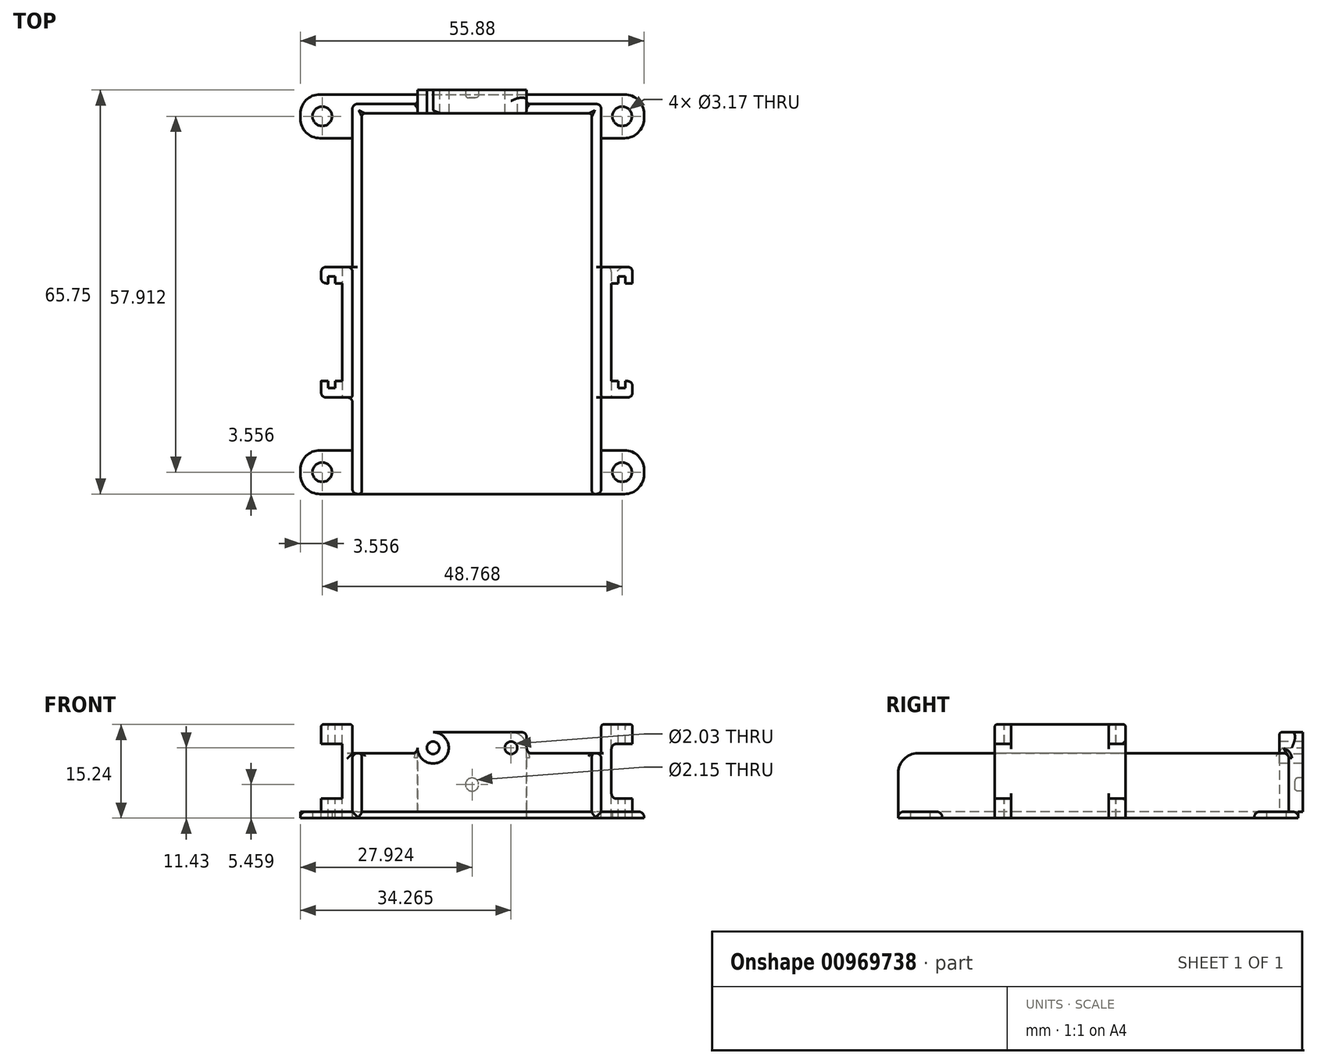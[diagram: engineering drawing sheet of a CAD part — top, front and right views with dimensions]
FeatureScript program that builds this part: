
annotation { "Feature Type Name" : "Feature", "Feature Type Description" : "" }
export const myFeature = defineFeature(function(context is Context, id is Id, definition is map)
    precondition{}
    {
        {
            var Q0;
            Q0=qCreatedBy(makeId("Top.planeOp"),FACE);
            var sketch = newSketch(context, id + "F0", { "sketchPlane" : qUnion([Q0])});
            skLineSegment(sketch, "E0", {"start": v(0, -32.35) * mm, "end": v(-27.94, -32.35) * mm});
            skLineSegment(sketch, "E1", {"start": v(-27.94, -32.35) * mm, "end": v(-27.94, -25.24) * mm});
            skLineSegment(sketch, "E2", {"start": v(-27.94, 32.67) * mm, "end": v(27.94, 32.67) * mm});
            skLineSegment(sketch, "E3", {"start": v(27.94, 32.67) * mm, "end": v(27.94, 25.56) * mm});
            skLineSegment(sketch, "E4", {"start": v(27.94, -32.35) * mm, "end": v(0, -32.35) * mm});
            skLineSegment(sketch, "E5", {"start": v(0, -32.35) * mm, "end": v(0, 32.67) * mm, "construction": true});
            skLineSegment(sketch, "E6", {"start": v(-29.38, 29.12) * mm, "end": v(30.41, 29.12) * mm, "construction": true});
            skLineSegment(sketch, "E7", {"start": v(-30.17, -28.8) * mm, "end": v(31.36, -28.8) * mm, "construction": true});
            skLineSegment(sketch, "E8", {"start": v(-24.38, 34.73) * mm, "end": v(-24.38, -35.44) * mm, "construction": true});
            skLineSegment(sketch, "E9", {"start": v(24.38, 35.22) * mm, "end": v(24.38, -36.91) * mm, "construction": true});
            skCircle(sketch, "E10", {"center": v(-24.38, 29.12) * mm, "radius": 1.59 * mm});
            skCircle(sketch, "E11", {"center": v(24.38, 29.12) * mm, "radius": 1.59 * mm});
            skCircle(sketch, "E12", {"center": v(-24.38, -28.8) * mm, "radius": 1.59 * mm});
            skCircle(sketch, "E13", {"center": v(24.38, -28.8) * mm, "radius": 1.59 * mm});
            skLineSegment(sketch, "E14.MirrorCS", {"start": v(27.94, -25.24) * mm, "end": v(21, -25.24) * mm});
            skLineSegment(sketch, "E15.MirrorCS", {"start": v(-27.94, 25.56) * mm, "end": v(-19.47, 25.56) * mm});
            skLineSegment(sketch, "E16", {"start": v(21, -25.24) * mm, "end": v(21, 25.56) * mm});
            skLineSegment(sketch, "E17", {"start": v(-19.47, 25.56) * mm, "end": v(-19.47, -25.24) * mm});
            skLineSegment(sketch, "E18.trimOffspring", {"start": v(-27.94, 25.56) * mm, "end": v(-27.94, 32.67) * mm});
            skLineSegment(sketch, "E19.trimOffspring", {"start": v(27.94, -25.24) * mm, "end": v(27.94, -32.35) * mm});
            skLineSegment(sketch, "E20.trimOffspring", {"start": v(21, 25.56) * mm, "end": v(27.94, 25.56) * mm});
            skLineSegment(sketch, "E21", {"start": v(-27.94, -25.24) * mm, "end": v(-19.47, -25.24) * mm});
            skSolve(sketch);
        }
        {
            var Q0;
            Q0 = qSketchRegion(id + "F0", true);
            extrude(context, id + "F1", {"entities" : qUnion([Q0]), "depth" : 1.02 * mm, "offsetDistance" : 25.4 * mm});
        }
        {
            var Q0;
            Q0=makeQuery(id+"F1.opExtrude","CAP_FACE",FACE,{"disambiguationData":[OSD([sQuery(id+"F0.wireOp",EDGE,"E0"),sQuery(id+"F0.wireOp",EDGE,"E1"),sQuery(id+"F0.wireOp",EDGE,"E2"),sQuery(id+"F0.wireOp",EDGE,"E3"),sQuery(id+"F0.wireOp",EDGE,"E4"),sQuery(id+"F0.wireOp",EDGE,"E10"),sQuery(id+"F0.wireOp",EDGE,"E11"),sQuery(id+"F0.wireOp",EDGE,"E12"),sQuery(id+"F0.wireOp",EDGE,"E13"),sQuery(id+"F0.wireOp",EDGE,"E14.MirrorCS"),sQuery(id+"F0.wireOp",EDGE,"E15.MirrorCS"),sQuery(id+"F0.wireOp",EDGE,"E16"),sQuery(id+"F0.wireOp",EDGE,"E17"),sQuery(id+"F0.wireOp",EDGE,"E18.trimOffspring"),sQuery(id+"F0.wireOp",EDGE,"E19.trimOffspring"),sQuery(id+"F0.wireOp",EDGE,"E20.trimOffspring"),sQuery(id+"F0.wireOp",EDGE,"E21")])],"isStart":false});
            var sketch = newSketch(context, id + "F2", { "sketchPlane" : qUnion([Q0])});
            skLineSegment(sketch, "E22", {"start": v(-19.47, 0) * mm, "end": v(-19.47, 31.13) * mm});
            skLineSegment(sketch, "E23", {"start": v(21, 0.16) * mm, "end": v(21, 31.13) * mm});
            skLineSegment(sketch, "E24", {"start": v(-19.47, 0) * mm, "end": v(-19.47, -32.35) * mm});
            skLineSegment(sketch, "E25", {"start": v(-19.47, -32.35) * mm, "end": v(-17.94, -32.35) * mm});
            skLineSegment(sketch, "E26", {"start": v(-17.94, -32.35) * mm, "end": v(-17.94, 29.59) * mm});
            skLineSegment(sketch, "E27", {"start": v(-17.94, 29.59) * mm, "end": v(19.47, 29.59) * mm});
            skLineSegment(sketch, "E28", {"start": v(19.47, 29.59) * mm, "end": v(19.47, -32.35) * mm});
            skLineSegment(sketch, "E29", {"start": v(19.47, -32.35) * mm, "end": v(21, -32.35) * mm});
            skLineSegment(sketch, "E30", {"start": v(21, -32.35) * mm, "end": v(21, 0.16) * mm});
            skLineSegment(sketch, "E31", {"start": v(0, 31.13) * mm, "end": v(-19.47, 31.13) * mm});
            skLineSegment(sketch, "E32", {"start": v(-19.47, 31.13) * mm, "end": v(0, 31.13) * mm});
            skLineSegment(sketch, "E33", {"start": v(0, 31.13) * mm, "end": v(21, 31.13) * mm});
            skSolve(sketch);
        }
        {
            var Q0;
            {var subQ0=sQuery(id+"F2.wireOp",EDGE,"E25");Q0=makeQuery(id+"F2.imprint","IMPRINT",FACE,{"disambiguationData":[TD([[makeQuery(id+"F2.imprint","IMPRINT",EDGE,{"derivedFrom":subQ0}),-1.0]])]});}
            extrude(context, id + "F3", {"entities" : qUnion([Q0]), "operationType" : NewBodyOperationType.ADD, "depth" : 9.52 * mm, "offsetDistance" : 25.4 * mm});
        }
        {
            var Q0;
            Q0=makeQuery(id+"F3.boolean.opBoolean","MERGE",FACE,{"derivedFrom":[makeQuery(id+"F1.opExtrude","SWEPT_FACE",FACE,{"disambiguationData":[OSD([sQuery(id+"F0.wireOp",EDGE,"E17")])]}),makeQuery(id+"F3.opExtrude","SWEPT_FACE",FACE,{"disambiguationData":[OSD([sQuery(id+"F2.wireOp",EDGE,"E22"),sQuery(id+"F2.wireOp",EDGE,"E24")])]})]});
            var sketch = newSketch(context, id + "F4", { "sketchPlane" : qUnion([Q0])});
            skLineSegment(sketch, "E34.bottom", {"start": v(16.65, 0) * mm, "end": v(-4.6, 0) * mm});
            skLineSegment(sketch, "E34.top", {"start": v(16.65, 15.24) * mm, "end": v(-4.6, 15.24) * mm});
            skLineSegment(sketch, "E34.left", {"start": v(16.65, 0) * mm, "end": v(16.65, 15.24) * mm});
            skLineSegment(sketch, "E34.right", {"start": v(-4.6, 0) * mm, "end": v(-4.6, 15.24) * mm});
            skSolve(sketch);
        }
        {
            var Q0;
            {var subQ0=sQuery(id+"F4.wireOp",EDGE,"E34.top");Q0=makeQuery(id+"F4.imprint","IMPRINT",FACE,{"disambiguationData":[TD([[makeQuery(id+"F4.imprint","IMPRINT",EDGE,{"derivedFrom":subQ0}),1.0]])]});}
            var Q1;
            {var subQ1=sQuery(id+"F4.wireOp",EDGE,"E34.bottom");Q1=makeQuery(id+"F4.imprint","IMPRINT",FACE,{"disambiguationData":[TD([[makeQuery(id+"F4.imprint","IMPRINT",EDGE,{"derivedFrom":subQ1}),1.0]])]});}
            extrude(context, id + "F5", {"entities" : qUnion([Q0, Q1]), "operationType" : NewBodyOperationType.ADD, "depth" : 5.08 * mm, "offsetDistance" : 25.4 * mm});
        }
        {
            var Q0;
            Q0=makeQuery(id+"F5.opExtrude","SWEPT_FACE",FACE,{"disambiguationData":[OSD([sQuery(id+"F4.wireOp",EDGE,"E34.top")])]});
            var sketch = newSketch(context, id + "F6", { "sketchPlane" : qUnion([Q0])});
            skLineSegment(sketch, "E35", {"start": v(-24.55, 1.94) * mm, "end": v(-23.4, 1.94) * mm});
            skLineSegment(sketch, "E36", {"start": v(-23.4, 1.94) * mm, "end": v(-23.4, 3.08) * mm});
            skLineSegment(sketch, "E37", {"start": v(-23.4, 3.08) * mm, "end": v(-22.26, 3.08) * mm});
            skLineSegment(sketch, "E38", {"start": v(-22.26, 3.08) * mm, "end": v(-22.26, 1.94) * mm});
            skLineSegment(sketch, "E39", {"start": v(-22.26, 1.94) * mm, "end": v(-21.12, 1.94) * mm});
            skLineSegment(sketch, "E40", {"start": v(-21.12, 1.94) * mm, "end": v(-21.12, -13.94) * mm});
            skLineSegment(sketch, "E41", {"start": v(-21.12, -13.94) * mm, "end": v(-22.26, -13.94) * mm});
            skLineSegment(sketch, "E42", {"start": v(-22.26, -13.94) * mm, "end": v(-22.26, -15.08) * mm});
            skLineSegment(sketch, "E43", {"start": v(-22.26, -15.08) * mm, "end": v(-23.4, -15.08) * mm});
            skLineSegment(sketch, "E44", {"start": v(-23.4, -15.08) * mm, "end": v(-23.4, -13.94) * mm});
            skLineSegment(sketch, "E45", {"start": v(-23.4, -13.94) * mm, "end": v(-24.55, -13.94) * mm});
            skLineSegment(sketch, "E46", {"start": v(-24.55, -13.94) * mm, "end": v(-24.55, 1.94) * mm});
            skSolve(sketch);
        }
        {
            var Q0;
            Q0=makeQuery(id+"F6.imprint","IMPRINT",FACE,{"disambiguationData":[TD([[makeQuery(id+"F6.imprint","IMPRINT",EDGE,{"derivedFrom":sQuery(id+"F6.wireOp",EDGE,"E35")}),-1.0]])]});
            extrude(context, id + "F7", {"entities" : qUnion([Q0]), "operationType" : NewBodyOperationType.REMOVE, "oppositeDirection" : true, "depth" : 15.24 * mm, "offsetDistance" : 25.4 * mm});
        }
        {
            var Q0;
            Q0=makeQuery(id+"F3.opExtrude","SWEPT_FACE",FACE,{"disambiguationData":[OSD([sQuery(id+"F2.wireOp",EDGE,"E27")])]});
            var sketch = newSketch(context, id + "F8", { "sketchPlane" : qUnion([Q0])});
            skLineSegment(sketch, "E47", {"start": v(0.76, 1.02) * mm, "end": v(8.86, 1.02) * mm});
            skLineSegment(sketch, "E48", {"start": v(8.86, 1.02) * mm, "end": v(8.86, 13.97) * mm});
            skLineSegment(sketch, "E49", {"start": v(8.86, 13.97) * mm, "end": v(-8.9, 13.97) * mm});
            skLineSegment(sketch, "E50", {"start": v(-8.9, 13.97) * mm, "end": v(-8.9, 1.02) * mm});
            skLineSegment(sketch, "E51", {"start": v(-8.9, 1.02) * mm, "end": v(0.76, 1.02) * mm});
            skSolve(sketch);
        }
        {
            var Q0;
            {var subQ2=sQuery(id+"F8.wireOp",EDGE,"E47");Q0=makeQuery(id+"F8.imprint","IMPRINT",FACE,{"disambiguationData":[TD([[makeQuery(id+"F8.imprint","IMPRINT",EDGE,{"derivedFrom":subQ2}),1.0]])]});}
            var Q1;
            {var subQ0=sQuery(id+"F8.wireOp",EDGE,"E49");Q1=makeQuery(id+"F8.imprint","IMPRINT",FACE,{"disambiguationData":[TD([[makeQuery(id+"F8.imprint","IMPRINT",EDGE,{"derivedFrom":subQ0}),1.0]])]});}
            extrude(context, id + "F9", {"entities" : qUnion([Q0, Q1]), "operationType" : NewBodyOperationType.ADD, "depth" : -2.54 * mm, "offsetDistance" : 25.4 * mm});
        }
        {
            var Q0;
            Q0=makeQuery(id+"F9.opExtrude","CAP_FACE",FACE,{"disambiguationData":[OSD([sQuery(id+"F8.wireOp",EDGE,"E47"),sQuery(id+"F8.wireOp",EDGE,"E48"),sQuery(id+"F8.wireOp",EDGE,"E49"),sQuery(id+"F8.wireOp",EDGE,"E50"),sQuery(id+"F8.wireOp",EDGE,"E51")])],"isStart":false});
            var sketch = newSketch(context, id + "F10", { "sketchPlane" : qUnion([Q0])});
            skCircle(sketch, "E52", {"center": v(-6.32, 11.43) * mm, "radius": 1.02 * mm});
            skCircle(sketch, "E53", {"center": v(-6.32, 11.43) * mm, "radius": 2.54 * mm});
            skLineSegment(sketch, "E54", {"start": v(0.02, 13.97) * mm, "end": v(0.02, 1.02) * mm});
            skCircle(sketch, "E55", {"center": v(0.02, 5.46) * mm, "radius": 1.08 * mm});
            skCircle(sketch, "E56.MirrorC", {"center": v(6.36, 11.43) * mm, "radius": 1.02 * mm});
            skCircle(sketch, "E57.MirrorC", {"center": v(6.36, 11.43) * mm, "radius": 2.54 * mm});
            skSolve(sketch);
        }
        {
            var Q0;
            Q0=makeQuery(id+"F10.imprint","IMPRINT",FACE,{"disambiguationData":[TD([[makeQuery(id+"F10.imprint","IMPRINT",EDGE,{"derivedFrom":sQuery(id+"F10.wireOp",EDGE,"E52")}),-1.0]])]});
            var Q1;
            Q1=makeQuery(id+"F10.imprint","IMPRINT",FACE,{"disambiguationData":[TD([[makeQuery(id+"F10.imprint","IMPRINT",EDGE,{"derivedFrom":sQuery(id+"F10.wireOp",EDGE,"E56.MirrorC")}),1.0]])]});
            var Q2;
            {var subQ0=sQuery(id+"F10.wireOp",EDGE,"E55");var subQ1=sQuery(id+"F10.wireOp",EDGE,"E54");var subQ2=makeQuery(id+"F10.imprint","INTERSECT",VERTEX,{"disambiguationData":[OD(0.0)],"derivedFrom":[subQ1,subQ0]});Q2=makeQuery(id+"F10.imprint","IMPRINT",FACE,{"disambiguationData":[TD([[makeQuery(id+"F10.imprint","IMPRINT",EDGE,{"disambiguationData":[TD([[subQ2,-1.0]])],"derivedFrom":subQ1}),1.0]])]});}
            var Q3;
            {var subQ0=sQuery(id+"F10.wireOp",EDGE,"E55");var subQ1=sQuery(id+"F10.wireOp",EDGE,"E54");var subQ2=makeQuery(id+"F10.imprint","INTERSECT",VERTEX,{"disambiguationData":[OD(0.0)],"derivedFrom":[subQ1,subQ0]});Q3=makeQuery(id+"F10.imprint","IMPRINT",FACE,{"disambiguationData":[TD([[makeQuery(id+"F10.imprint","IMPRINT",EDGE,{"disambiguationData":[TD([[subQ2,-1.0]])],"derivedFrom":subQ1}),-1.0]])]});}
            extrude(context, id + "F11", {"entities" : qUnion([Q0, Q1, Q2, Q3]), "operationType" : NewBodyOperationType.ADD, "depth" : 1.27 * mm, "offsetDistance" : 25.4 * mm});
        }
        {
            var Q0;
            Q0=makeQuery(id+"F11.boolean.opBoolean","SPLIT",FACE,{"disambiguationData":[TD([makeQuery(id+"F11.opExtrude","SWEPT_FACE",FACE,{"disambiguationData":[OSD([sQuery(id+"F10.wireOp",EDGE,"E52")])]})])],"derivedFrom":makeQuery(id+"F9.opExtrude","CAP_FACE",FACE,{"disambiguationData":[OSD([sQuery(id+"F8.wireOp",EDGE,"E47"),sQuery(id+"F8.wireOp",EDGE,"E48"),sQuery(id+"F8.wireOp",EDGE,"E49"),sQuery(id+"F8.wireOp",EDGE,"E50"),sQuery(id+"F8.wireOp",EDGE,"E51")])],"isStart":false})});
            var Q1;
            Q1=makeQuery(id+"F11.boolean.opBoolean","SPLIT",FACE,{"disambiguationData":[TD([makeQuery(id+"F11.opExtrude","SWEPT_FACE",FACE,{"disambiguationData":[OSD([sQuery(id+"F10.wireOp",EDGE,"E56.MirrorC")])]})])],"derivedFrom":makeQuery(id+"F9.opExtrude","CAP_FACE",FACE,{"disambiguationData":[OSD([sQuery(id+"F8.wireOp",EDGE,"E47"),sQuery(id+"F8.wireOp",EDGE,"E48"),sQuery(id+"F8.wireOp",EDGE,"E49"),sQuery(id+"F8.wireOp",EDGE,"E50"),sQuery(id+"F8.wireOp",EDGE,"E51")])],"isStart":false})});
            extrude(context, id + "F12", {"entities" : qUnion([Q0, Q1]), "operationType" : NewBodyOperationType.REMOVE, "oppositeDirection" : true, "depth" : 2.54 * mm, "offsetDistance" : 25.4 * mm});
        }
        {
            var Q0;
            Q0=makeQuery(id+"F1.opExtrude","SWEPT_EDGE",EDGE,{"disambiguationData":[OSD([sQuery(id+"F0.wireOp",EDGE,"E2"),sQuery(id+"F0.wireOp",EDGE,"E18.trimOffspring")])]});
            var Q1;
            Q1=makeQuery(id+"F1.opExtrude","SWEPT_EDGE",EDGE,{"disambiguationData":[OSD([sQuery(id+"F0.wireOp",EDGE,"E15.MirrorCS"),sQuery(id+"F0.wireOp",EDGE,"E18.trimOffspring")])]});
            var Q2;
            Q2=makeQuery(id+"F1.opExtrude","SWEPT_EDGE",EDGE,{"disambiguationData":[OSD([sQuery(id+"F0.wireOp",EDGE,"E3"),sQuery(id+"F0.wireOp",EDGE,"E20.trimOffspring")])]});
            var Q3;
            Q3=makeQuery(id+"F1.opExtrude","SWEPT_EDGE",EDGE,{"disambiguationData":[OSD([sQuery(id+"F0.wireOp",EDGE,"E2"),sQuery(id+"F0.wireOp",EDGE,"E3")])]});
            var Q4;
            Q4=makeQuery(id+"F1.opExtrude","SWEPT_EDGE",EDGE,{"disambiguationData":[OSD([sQuery(id+"F0.wireOp",EDGE,"E4"),sQuery(id+"F0.wireOp",EDGE,"E19.trimOffspring")])]});
            var Q5;
            Q5=makeQuery(id+"F1.opExtrude","SWEPT_EDGE",EDGE,{"disambiguationData":[OSD([sQuery(id+"F0.wireOp",EDGE,"E14.MirrorCS"),sQuery(id+"F0.wireOp",EDGE,"E19.trimOffspring")])]});
            var Q6;
            Q6=makeQuery(id+"F1.opExtrude","SWEPT_EDGE",EDGE,{"disambiguationData":[OSD([sQuery(id+"F0.wireOp",EDGE,"E1"),sQuery(id+"F0.wireOp",EDGE,"E21")])]});
            var Q7;
            Q7=makeQuery(id+"F1.opExtrude","SWEPT_EDGE",EDGE,{"disambiguationData":[OSD([sQuery(id+"F0.wireOp",EDGE,"E0"),sQuery(id+"F0.wireOp",EDGE,"E1")])]});
            fillet(context, id + "F13", {"entities" : qUnion([Q0, Q1, Q2, Q3, Q4, Q5, Q6, Q7]), "radius" : 3.17 * mm, "tangentPropagation" : true, "allowEdgeOverflow" : false});
        }
        {
            var Q0;
            Q0=makeQuery(id+"F5.opExtrude","SWEPT_FACE",FACE,{"disambiguationData":[OSD([sQuery(id+"F4.wireOp",EDGE,"E34.left")])]});
            var sketch = newSketch(context, id + "F14", { "sketchPlane" : qUnion([Q0])});
            skLineSegment(sketch, "E58.bottom", {"start": v(-24.55, 12.07) * mm, "end": v(-21.12, 12.07) * mm});
            skLineSegment(sketch, "E58.top", {"start": v(-24.55, 3.17) * mm, "end": v(-21.12, 3.17) * mm});
            skLineSegment(sketch, "E58.left", {"start": v(-24.55, 12.07) * mm, "end": v(-24.55, 3.17) * mm});
            skLineSegment(sketch, "E58.right", {"start": v(-21.12, 12.07) * mm, "end": v(-21.12, 3.17) * mm});
            skSolve(sketch);
        }
        {
            var Q0;
            Q0=makeQuery(id+"F14.imprint","IMPRINT",FACE,{"disambiguationData":[TD([[makeQuery(id+"F14.imprint","IMPRINT",EDGE,{"derivedFrom":sQuery(id+"F14.wireOp",EDGE,"E58.bottom")}),-1.0]])]});
            extrude(context, id + "F15", {"entities" : qUnion([Q0]), "operationType" : NewBodyOperationType.REMOVE, "oppositeDirection" : true, "depth" : 25.4 * mm, "offsetDistance" : 25.4 * mm});
        }
        {
            var Q0;
            Q0=makeQuery(id+"F3.boolean.opBoolean","MERGE",FACE,{"derivedFrom":[makeQuery(id+"F1.opExtrude","SWEPT_FACE",FACE,{"disambiguationData":[OSD([sQuery(id+"F0.wireOp",EDGE,"E16")])]}),makeQuery(id+"F3.opExtrude","SWEPT_FACE",FACE,{"disambiguationData":[OSD([sQuery(id+"F2.wireOp",EDGE,"E23"),sQuery(id+"F2.wireOp",EDGE,"E30")])]})]});
            var sketch = newSketch(context, id + "F16", { "sketchPlane" : qUnion([Q0])});
            skLineSegment(sketch, "E59.bottom", {"start": v(-16.65, 0) * mm, "end": v(4.6, 0) * mm});
            skLineSegment(sketch, "E59.top", {"start": v(-16.65, 15.24) * mm, "end": v(4.6, 15.24) * mm});
            skLineSegment(sketch, "E59.left", {"start": v(-16.65, 0) * mm, "end": v(-16.65, 15.24) * mm});
            skLineSegment(sketch, "E59.right", {"start": v(4.6, 0) * mm, "end": v(4.6, 15.24) * mm});
            skSolve(sketch);
        }
        {
            var Q0;
            {var subQ0=sQuery(id+"F16.wireOp",EDGE,"E59.bottom");Q0=makeQuery(id+"F16.imprint","IMPRINT",FACE,{"disambiguationData":[TD([[makeQuery(id+"F16.imprint","IMPRINT",EDGE,{"derivedFrom":subQ0}),1.0]])]});}
            var Q1;
            {var subQ0=sQuery(id+"F16.wireOp",EDGE,"E59.top");Q1=makeQuery(id+"F16.imprint","IMPRINT",FACE,{"disambiguationData":[TD([[makeQuery(id+"F16.imprint","IMPRINT",EDGE,{"derivedFrom":subQ0}),-1.0]])]});}
            extrude(context, id + "F17", {"entities" : qUnion([Q0, Q1]), "operationType" : NewBodyOperationType.ADD, "depth" : 5.08 * mm, "offsetDistance" : 25.4 * mm});
        }
        {
            var Q0;
            Q0=makeQuery(id+"F17.opExtrude","SWEPT_FACE",FACE,{"disambiguationData":[OSD([sQuery(id+"F16.wireOp",EDGE,"E59.top")])]});
            var sketch = newSketch(context, id + "F18", { "sketchPlane" : qUnion([Q0])});
            skLineSegment(sketch, "E60", {"start": v(26.07, -13.99) * mm, "end": v(24.93, -13.99) * mm});
            skLineSegment(sketch, "E61", {"start": v(24.93, -13.99) * mm, "end": v(24.93, -15.13) * mm});
            skLineSegment(sketch, "E62", {"start": v(24.93, -15.13) * mm, "end": v(23.79, -15.13) * mm});
            skLineSegment(sketch, "E63", {"start": v(23.79, -15.13) * mm, "end": v(23.79, -13.99) * mm});
            skLineSegment(sketch, "E64", {"start": v(23.79, -13.99) * mm, "end": v(22.64, -13.99) * mm});
            skLineSegment(sketch, "E65", {"start": v(22.64, -13.99) * mm, "end": v(22.64, 1.89) * mm});
            skLineSegment(sketch, "E66", {"start": v(22.64, 1.89) * mm, "end": v(23.79, 1.89) * mm});
            skLineSegment(sketch, "E67", {"start": v(23.79, 1.89) * mm, "end": v(23.79, 3.03) * mm});
            skLineSegment(sketch, "E68", {"start": v(23.79, 3.03) * mm, "end": v(24.93, 3.03) * mm});
            skLineSegment(sketch, "E69", {"start": v(24.93, 3.03) * mm, "end": v(24.93, 1.89) * mm});
            skLineSegment(sketch, "E70", {"start": v(24.93, 1.89) * mm, "end": v(26.07, 1.89) * mm});
            skLineSegment(sketch, "E71", {"start": v(26.07, 1.89) * mm, "end": v(26.07, -13.99) * mm});
            skSolve(sketch);
        }
        {
            var Q0;
            Q0=makeQuery(id+"F18.imprint","IMPRINT",FACE,{"disambiguationData":[TD([[makeQuery(id+"F18.imprint","IMPRINT",EDGE,{"derivedFrom":sQuery(id+"F18.wireOp",EDGE,"E60")}),-1.0]])]});
            extrude(context, id + "F19", {"entities" : qUnion([Q0]), "operationType" : NewBodyOperationType.REMOVE, "oppositeDirection" : true, "depth" : 25.4 * mm, "offsetDistance" : 25.4 * mm});
        }
        {
            var Q0;
            Q0=makeQuery(id+"F17.opExtrude","SWEPT_FACE",FACE,{"disambiguationData":[OSD([sQuery(id+"F16.wireOp",EDGE,"E59.left")])]});
            var sketch = newSketch(context, id + "F20", { "sketchPlane" : qUnion([Q0])});
            skLineSegment(sketch, "E72.bottom", {"start": v(26.07, 12.07) * mm, "end": v(22.64, 12.07) * mm});
            skLineSegment(sketch, "E72.top", {"start": v(26.07, 3.18) * mm, "end": v(22.64, 3.18) * mm});
            skLineSegment(sketch, "E72.left", {"start": v(26.07, 12.07) * mm, "end": v(26.07, 3.18) * mm});
            skLineSegment(sketch, "E72.right", {"start": v(22.64, 12.07) * mm, "end": v(22.64, 3.18) * mm});
            skSolve(sketch);
        }
        {
            var Q0;
            Q0=makeQuery(id+"F20.imprint","IMPRINT",FACE,{"disambiguationData":[TD([[makeQuery(id+"F20.imprint","IMPRINT",EDGE,{"derivedFrom":sQuery(id+"F20.wireOp",EDGE,"E72.bottom")}),1.0]])]});
            extrude(context, id + "F21", {"entities" : qUnion([Q0]), "operationType" : NewBodyOperationType.REMOVE, "oppositeDirection" : true, "depth" : 25.4 * mm, "offsetDistance" : 25.4 * mm});
        }
        {
            var Q0;
            Q0=makeQuery(id+"F3.opExtrude","CAP_EDGE",EDGE,{"disambiguationData":[OSD([sQuery(id+"F2.wireOp",EDGE,"E29")])],"isStart":false});
            var Q1;
            Q1=makeQuery(id+"F3.opExtrude","CAP_EDGE",EDGE,{"disambiguationData":[OSD([sQuery(id+"F2.wireOp",EDGE,"E25")])],"isStart":false});
            fillet(context, id + "F22", {"entities" : qUnion([Q0, Q1]), "radius" : 3.17 * mm, "tangentPropagation" : true, "allowEdgeOverflow" : false});
        }
        {
            var Q0;
            {var subQ1=sQuery(id+"F0.wireOp",EDGE,"E16");var subQ2=sQuery(id+"F0.wireOp",EDGE,"E4");var subQ3=sQuery(id+"F0.wireOp",EDGE,"E0");Q0=makeQuery(id+"F3.boolean.opBoolean","SPLIT",EDGE,{"disambiguationData":[TD([makeQuery(id+"F1.opExtrude","SWEPT_FACE",FACE,{"disambiguationData":[OSD([subQ1])]})])],"derivedFrom":makeQuery(id+"F1.opExtrude","CAP_EDGE",EDGE,{"disambiguationData":[OSD([subQ3,subQ2])],"isStart":false})});}
            var Q1;
            Q1=makeQuery(id+"F3.opExtrude","SWEPT_EDGE",EDGE,{"disambiguationData":[OSD([sQuery(id+"F0.wireOp",EDGE,"E0"),sQuery(id+"F0.wireOp",EDGE,"E4"),sQuery(id+"F2.wireOp",EDGE,"E29"),sQuery(id+"F2.wireOp",EDGE,"E30")])]});
            var Q2;
            Q2=makeQuery(id+"F21.boolean.opBoolean","COPY",EDGE,{"derivedFrom":makeQuery(id+"F21.opExtrude","CAP_EDGE",EDGE,{"disambiguationData":[OSD([sQuery(id+"F20.wireOp",EDGE,"E72.right")])],"isStart":true})});
            var Q3;
            {var subQ0=sQuery(id+"F16.wireOp",EDGE,"E59.left");Q3=makeQuery(id+"F21.boolean.opBoolean","SPLIT",EDGE,{"disambiguationData":[TD([makeQuery(id+"F5.opExtrude","SWEPT_FACE",FACE,{"disambiguationData":[OSD([sQuery(id+"F4.wireOp",EDGE,"E34.bottom")])]})])],"derivedFrom":makeQuery(id+"F17.opExtrude","CAP_EDGE",EDGE,{"disambiguationData":[OSD([subQ0])],"isStart":false})});}
            var Q4;
            {var subQ0=sQuery(id+"F16.wireOp",EDGE,"E59.top");var subQ2=sQuery(id+"F18.wireOp",EDGE,"E60");Q4=makeQuery(id+"F21.boolean.opBoolean","SPLIT",EDGE,{"disambiguationData":[TD([makeQuery(id+"F5.opExtrude","SWEPT_FACE",FACE,{"disambiguationData":[OSD([sQuery(id+"F4.wireOp",EDGE,"E34.bottom")])]})])],"derivedFrom":makeQuery(id+"F19.boolean.opBoolean","COPY",EDGE,{"derivedFrom":makeQuery(id+"F19.opExtrude","SWEPT_EDGE",EDGE,{"disambiguationData":[OSD([subQ0,subQ2,sQuery(id+"F18.wireOp",EDGE,"E71")])]})})});}
            var Q5;
            {var subQ0=sQuery(id+"F16.wireOp",EDGE,"E59.top");var subQ2=sQuery(id+"F18.wireOp",EDGE,"E70");Q5=makeQuery(id+"F21.boolean.opBoolean","SPLIT",EDGE,{"disambiguationData":[TD([makeQuery(id+"F5.opExtrude","SWEPT_FACE",FACE,{"disambiguationData":[OSD([sQuery(id+"F4.wireOp",EDGE,"E34.bottom")])]})])],"derivedFrom":makeQuery(id+"F19.boolean.opBoolean","COPY",EDGE,{"derivedFrom":makeQuery(id+"F19.opExtrude","SWEPT_EDGE",EDGE,{"disambiguationData":[OSD([subQ0,subQ2,sQuery(id+"F18.wireOp",EDGE,"E71")])]})})});}
            var Q6;
            {var subQ0=sQuery(id+"F16.wireOp",EDGE,"E59.right");Q6=makeQuery(id+"F21.boolean.opBoolean","SPLIT",EDGE,{"disambiguationData":[TD([makeQuery(id+"F5.opExtrude","SWEPT_FACE",FACE,{"disambiguationData":[OSD([sQuery(id+"F4.wireOp",EDGE,"E34.bottom")])]})])],"derivedFrom":makeQuery(id+"F17.opExtrude","CAP_EDGE",EDGE,{"disambiguationData":[OSD([subQ0])],"isStart":false})});}
            var Q7;
            Q7=makeQuery(id+"F21.boolean.opBoolean","INTERSECT",EDGE,{"derivedFrom":[makeQuery(id+"F17.opExtrude","SWEPT_FACE",FACE,{"disambiguationData":[OSD([sQuery(id+"F16.wireOp",EDGE,"E59.right")])]}),makeQuery(id+"F21.opExtrude","SWEPT_FACE",FACE,{"disambiguationData":[OSD([sQuery(id+"F20.wireOp",EDGE,"E72.right")])]})]});
            var Q8;
            {var subQ0=sQuery(id+"F16.wireOp",EDGE,"E59.right");var subQ1=sQuery(id+"F16.wireOp",EDGE,"E59.top");Q8=makeQuery(id+"F21.boolean.opBoolean","SPLIT",EDGE,{"disambiguationData":[TD([makeQuery(id+"F17.opExtrude","SWEPT_FACE",FACE,{"disambiguationData":[OSD([subQ1])]})])],"derivedFrom":makeQuery(id+"F17.opExtrude","CAP_EDGE",EDGE,{"disambiguationData":[OSD([subQ0])],"isStart":false})});}
            var Q9;
            {var subQ0=sQuery(id+"F16.wireOp",EDGE,"E59.top");var subQ1=sQuery(id+"F18.wireOp",EDGE,"E70");Q9=makeQuery(id+"F21.boolean.opBoolean","SPLIT",EDGE,{"disambiguationData":[TD([makeQuery(id+"F17.opExtrude","SWEPT_FACE",FACE,{"disambiguationData":[OSD([subQ0])]})])],"derivedFrom":makeQuery(id+"F19.boolean.opBoolean","COPY",EDGE,{"derivedFrom":makeQuery(id+"F19.opExtrude","SWEPT_EDGE",EDGE,{"disambiguationData":[OSD([subQ0,subQ1,sQuery(id+"F18.wireOp",EDGE,"E71")])]})})});}
            var Q10;
            {var subQ0=sQuery(id+"F16.wireOp",EDGE,"E59.top");var subQ1=sQuery(id+"F18.wireOp",EDGE,"E60");Q10=makeQuery(id+"F21.boolean.opBoolean","SPLIT",EDGE,{"disambiguationData":[TD([makeQuery(id+"F17.opExtrude","SWEPT_FACE",FACE,{"disambiguationData":[OSD([subQ0])]})])],"derivedFrom":makeQuery(id+"F19.boolean.opBoolean","COPY",EDGE,{"derivedFrom":makeQuery(id+"F19.opExtrude","SWEPT_EDGE",EDGE,{"disambiguationData":[OSD([subQ0,subQ1,sQuery(id+"F18.wireOp",EDGE,"E71")])]})})});}
            var Q11;
            {var subQ0=sQuery(id+"F16.wireOp",EDGE,"E59.left");var subQ1=sQuery(id+"F16.wireOp",EDGE,"E59.top");Q11=makeQuery(id+"F21.boolean.opBoolean","SPLIT",EDGE,{"disambiguationData":[TD([makeQuery(id+"F17.opExtrude","SWEPT_FACE",FACE,{"disambiguationData":[OSD([subQ1])]})])],"derivedFrom":makeQuery(id+"F17.opExtrude","CAP_EDGE",EDGE,{"disambiguationData":[OSD([subQ0])],"isStart":false})});}
            var Q12;
            {var subQ0=sQuery(id+"F20.wireOp",EDGE,"E72.top");var subQ1=sQuery(id+"F20.wireOp",EDGE,"E72.right");Q12=makeQuery(id+"F21.boolean.opBoolean","COPY",EDGE,{"disambiguationData":[TD([makeQuery(id+"F17.opExtrude","SWEPT_FACE",FACE,{"disambiguationData":[OSD([sQuery(id+"F16.wireOp",EDGE,"E59.left")])]})])],"derivedFrom":makeQuery(id+"F21.opExtrude","SWEPT_EDGE",EDGE,{"disambiguationData":[OSD([subQ0,subQ1])]})});}
            var Q13;
            {var subQ0=sQuery(id+"F20.wireOp",EDGE,"E72.top");var subQ1=sQuery(id+"F20.wireOp",EDGE,"E72.right");Q13=makeQuery(id+"F21.boolean.opBoolean","COPY",EDGE,{"disambiguationData":[TD([makeQuery(id+"F17.opExtrude","SWEPT_FACE",FACE,{"disambiguationData":[OSD([sQuery(id+"F16.wireOp",EDGE,"E59.right")])]})])],"derivedFrom":makeQuery(id+"F21.opExtrude","SWEPT_EDGE",EDGE,{"disambiguationData":[OSD([subQ0,subQ1])]})});}
            var Q14;
            {var subQ0=sQuery(id+"F20.wireOp",EDGE,"E72.bottom");var subQ1=sQuery(id+"F20.wireOp",EDGE,"E72.right");Q14=makeQuery(id+"F21.boolean.opBoolean","COPY",EDGE,{"disambiguationData":[TD([makeQuery(id+"F17.opExtrude","SWEPT_FACE",FACE,{"disambiguationData":[OSD([sQuery(id+"F16.wireOp",EDGE,"E59.right")])]})])],"derivedFrom":makeQuery(id+"F21.opExtrude","SWEPT_EDGE",EDGE,{"disambiguationData":[OSD([subQ0,subQ1])]})});}
            var Q15;
            {var subQ0=sQuery(id+"F20.wireOp",EDGE,"E72.bottom");var subQ1=sQuery(id+"F20.wireOp",EDGE,"E72.right");Q15=makeQuery(id+"F21.boolean.opBoolean","COPY",EDGE,{"disambiguationData":[TD([makeQuery(id+"F17.opExtrude","SWEPT_FACE",FACE,{"disambiguationData":[OSD([sQuery(id+"F16.wireOp",EDGE,"E59.left")])]})])],"derivedFrom":makeQuery(id+"F21.opExtrude","SWEPT_EDGE",EDGE,{"disambiguationData":[OSD([subQ0,subQ1])]})});}
            var Q16;
            Q16=makeQuery(id+"F3.opExtrude","SWEPT_EDGE",EDGE,{"disambiguationData":[OSD([sQuery(id+"F2.wireOp",EDGE,"E23"),sQuery(id+"F2.wireOp",EDGE,"E33")])]});
            fillet(context, id + "F23", {"entities" : qUnion([Q0, Q1, Q2, Q3, Q4, Q5, Q6, Q7, Q8, Q9, Q10, Q11, Q12, Q13, Q14, Q15, Q16]), "radius" : 0.81 * mm, "tangentPropagation" : true, "allowEdgeOverflow" : false});
        }
        {
            var Q0;
            Q0=makeQuery(id+"F1.opExtrude","CAP_EDGE",EDGE,{"disambiguationData":[OSD([sQuery(id+"F0.wireOp",EDGE,"E20.trimOffspring")])],"isStart":false});
            var Q1;
            {var subQ1=sQuery(id+"F0.wireOp",EDGE,"E4");var subQ2=sQuery(id+"F0.wireOp",EDGE,"E0");var subQ3=sQuery(id+"F0.wireOp",EDGE,"E1");Q1=makeQuery(id+"F3.boolean.opBoolean","SPLIT",EDGE,{"disambiguationData":[TD([makeQuery(id+"F1.opExtrude","SWEPT_FACE",FACE,{"disambiguationData":[OSD([subQ3])]})])],"derivedFrom":makeQuery(id+"F1.opExtrude","CAP_EDGE",EDGE,{"disambiguationData":[OSD([subQ2,subQ1])],"isStart":false})});}
            var Q2;
            {var subQ0=sQuery(id+"F0.wireOp",EDGE,"E4");var subQ1=sQuery(id+"F0.wireOp",EDGE,"E0");Q2=makeQuery(id+"F3.boolean.opBoolean","SPLIT",EDGE,{"disambiguationData":[TD([makeQuery(id+"F3.opExtrude","SWEPT_FACE",FACE,{"disambiguationData":[OSD([sQuery(id+"F2.wireOp",EDGE,"E26")])]})])],"derivedFrom":makeQuery(id+"F1.opExtrude","CAP_EDGE",EDGE,{"disambiguationData":[OSD([subQ1,subQ0])],"isStart":false})});}
            var Q3;
            {var subQ0=sQuery(id+"F4.wireOp",EDGE,"E34.left");var subQ1=sQuery(id+"F4.wireOp",EDGE,"E34.top");Q3=makeQuery(id+"F15.boolean.opBoolean","SPLIT",EDGE,{"disambiguationData":[TD([makeQuery(id+"F5.opExtrude","SWEPT_FACE",FACE,{"disambiguationData":[OSD([subQ1])]})])],"derivedFrom":makeQuery(id+"F5.opExtrude","CAP_EDGE",EDGE,{"disambiguationData":[OSD([subQ0])],"isStart":false})});}
            var Q4;
            {var subQ0=sQuery(id+"F4.wireOp",EDGE,"E34.left");var subQ1=sQuery(id+"F4.wireOp",EDGE,"E34.bottom");Q4=makeQuery(id+"F15.boolean.opBoolean","SPLIT",EDGE,{"disambiguationData":[TD([makeQuery(id+"F5.opExtrude","SWEPT_FACE",FACE,{"disambiguationData":[OSD([subQ1])]})])],"derivedFrom":makeQuery(id+"F5.opExtrude","CAP_EDGE",EDGE,{"disambiguationData":[OSD([subQ0])],"isStart":false})});}
            var Q5;
            {var subQ0=sQuery(id+"F4.wireOp",EDGE,"E34.top");var subQ1=sQuery(id+"F6.wireOp",EDGE,"E45");Q5=makeQuery(id+"F15.boolean.opBoolean","SPLIT",EDGE,{"disambiguationData":[TD([makeQuery(id+"F5.opExtrude","SWEPT_FACE",FACE,{"disambiguationData":[OSD([subQ0])]})])],"derivedFrom":makeQuery(id+"F7.boolean.opBoolean","COPY",EDGE,{"derivedFrom":makeQuery(id+"F7.opExtrude","SWEPT_EDGE",EDGE,{"disambiguationData":[OSD([subQ0,subQ1,sQuery(id+"F6.wireOp",EDGE,"E46")])]})})});}
            var Q6;
            {var subQ0=sQuery(id+"F4.wireOp",EDGE,"E34.top");var subQ1=sQuery(id+"F4.wireOp",EDGE,"E34.bottom");var subQ2=sQuery(id+"F6.wireOp",EDGE,"E45");Q6=makeQuery(id+"F15.boolean.opBoolean","SPLIT",EDGE,{"disambiguationData":[TD([makeQuery(id+"F5.opExtrude","SWEPT_FACE",FACE,{"disambiguationData":[OSD([subQ1])]})])],"derivedFrom":makeQuery(id+"F7.boolean.opBoolean","COPY",EDGE,{"derivedFrom":makeQuery(id+"F7.opExtrude","SWEPT_EDGE",EDGE,{"disambiguationData":[OSD([subQ0,subQ2,sQuery(id+"F6.wireOp",EDGE,"E46")])]})})});}
            var Q7;
            {var subQ0=sQuery(id+"F4.wireOp",EDGE,"E34.top");var subQ1=sQuery(id+"F4.wireOp",EDGE,"E34.bottom");var subQ2=sQuery(id+"F6.wireOp",EDGE,"E35");Q7=makeQuery(id+"F15.boolean.opBoolean","SPLIT",EDGE,{"disambiguationData":[TD([makeQuery(id+"F5.opExtrude","SWEPT_FACE",FACE,{"disambiguationData":[OSD([subQ1])]})])],"derivedFrom":makeQuery(id+"F7.boolean.opBoolean","COPY",EDGE,{"derivedFrom":makeQuery(id+"F7.opExtrude","SWEPT_EDGE",EDGE,{"disambiguationData":[OSD([subQ0,subQ2,sQuery(id+"F6.wireOp",EDGE,"E46")])]})})});}
            var Q8;
            {var subQ0=sQuery(id+"F4.wireOp",EDGE,"E34.right");var subQ1=sQuery(id+"F4.wireOp",EDGE,"E34.bottom");Q8=makeQuery(id+"F15.boolean.opBoolean","SPLIT",EDGE,{"disambiguationData":[TD([makeQuery(id+"F5.opExtrude","SWEPT_FACE",FACE,{"disambiguationData":[OSD([subQ1])]})])],"derivedFrom":makeQuery(id+"F5.opExtrude","CAP_EDGE",EDGE,{"disambiguationData":[OSD([subQ0])],"isStart":false})});}
            var Q9;
            {var subQ0=sQuery(id+"F4.wireOp",EDGE,"E34.top");var subQ1=sQuery(id+"F6.wireOp",EDGE,"E35");Q9=makeQuery(id+"F15.boolean.opBoolean","SPLIT",EDGE,{"disambiguationData":[TD([makeQuery(id+"F5.opExtrude","SWEPT_FACE",FACE,{"disambiguationData":[OSD([subQ0])]})])],"derivedFrom":makeQuery(id+"F7.boolean.opBoolean","COPY",EDGE,{"derivedFrom":makeQuery(id+"F7.opExtrude","SWEPT_EDGE",EDGE,{"disambiguationData":[OSD([subQ0,subQ1,sQuery(id+"F6.wireOp",EDGE,"E46")])]})})});}
            var Q10;
            {var subQ0=sQuery(id+"F4.wireOp",EDGE,"E34.right");var subQ1=sQuery(id+"F4.wireOp",EDGE,"E34.top");Q10=makeQuery(id+"F15.boolean.opBoolean","SPLIT",EDGE,{"disambiguationData":[TD([makeQuery(id+"F5.opExtrude","SWEPT_FACE",FACE,{"disambiguationData":[OSD([subQ1])]})])],"derivedFrom":makeQuery(id+"F5.opExtrude","CAP_EDGE",EDGE,{"disambiguationData":[OSD([subQ0])],"isStart":false})});}
            fillet(context, id + "F24", {"entities" : qUnion([Q0, Q1, Q2, Q3, Q4, Q5, Q6, Q7, Q8, Q9, Q10]), "radius" : 0.81 * mm, "tangentPropagation" : true, "allowEdgeOverflow" : false});
        }
        {
            var Q0;
            {var subQ0=sQuery(id+"F4.wireOp",EDGE,"E34.left");Q0=makeQuery(id+"F5.boolean.opBoolean","SPLIT",EDGE,{"disambiguationData":[topologyDisambiguationEdgeConnected([makeQuery(id+"F1.opExtrude","SWEPT_FACE",FACE,{"disambiguationData":[OSD([sQuery(id+"F0.wireOp",EDGE,"E17")])]})])],"derivedFrom":makeQuery(id+"F5.opExtrude","CAP_EDGE",EDGE,{"disambiguationData":[OSD([subQ0])],"isStart":true})});}
            var Q1;
            {var subQ0=sQuery(id+"F4.wireOp",EDGE,"E34.right");Q1=makeQuery(id+"F5.boolean.opBoolean","SPLIT",EDGE,{"disambiguationData":[topologyDisambiguationEdgeConnected([makeQuery(id+"F1.opExtrude","SWEPT_FACE",FACE,{"disambiguationData":[OSD([sQuery(id+"F0.wireOp",EDGE,"E17")])]})])],"derivedFrom":makeQuery(id+"F5.opExtrude","CAP_EDGE",EDGE,{"disambiguationData":[OSD([subQ0])],"isStart":true})});}
            var Q2;
            Q2=makeQuery(id+"F9.boolean.opBoolean","INTERSECT",EDGE,{"derivedFrom":[makeQuery(id+"F3.opExtrude","CAP_FACE",FACE,{"disambiguationData":[OSD([sQuery(id+"F2.wireOp",EDGE,"E22"),sQuery(id+"F2.wireOp",EDGE,"E23"),sQuery(id+"F2.wireOp",EDGE,"E24"),sQuery(id+"F2.wireOp",EDGE,"E25"),sQuery(id+"F2.wireOp",EDGE,"E26"),sQuery(id+"F2.wireOp",EDGE,"E27"),sQuery(id+"F2.wireOp",EDGE,"E28"),sQuery(id+"F2.wireOp",EDGE,"E29"),sQuery(id+"F2.wireOp",EDGE,"E30"),sQuery(id+"F2.wireOp",EDGE,"E32"),sQuery(id+"F2.wireOp",EDGE,"E33")])],"isStart":false}),makeQuery(id+"F9.opExtrude","SWEPT_FACE",FACE,{"disambiguationData":[OSD([sQuery(id+"F8.wireOp",EDGE,"E50")])]})]});
            var Q3;
            Q3=makeQuery(id+"F9.boolean.opBoolean","INTERSECT",EDGE,{"derivedFrom":[makeQuery(id+"F3.opExtrude","CAP_FACE",FACE,{"disambiguationData":[OSD([sQuery(id+"F2.wireOp",EDGE,"E22"),sQuery(id+"F2.wireOp",EDGE,"E23"),sQuery(id+"F2.wireOp",EDGE,"E24"),sQuery(id+"F2.wireOp",EDGE,"E25"),sQuery(id+"F2.wireOp",EDGE,"E26"),sQuery(id+"F2.wireOp",EDGE,"E27"),sQuery(id+"F2.wireOp",EDGE,"E28"),sQuery(id+"F2.wireOp",EDGE,"E29"),sQuery(id+"F2.wireOp",EDGE,"E30"),sQuery(id+"F2.wireOp",EDGE,"E32"),sQuery(id+"F2.wireOp",EDGE,"E33")])],"isStart":false}),makeQuery(id+"F9.opExtrude","SWEPT_FACE",FACE,{"disambiguationData":[OSD([sQuery(id+"F8.wireOp",EDGE,"E48")])]})]});
            var Q4;
            Q4=makeQuery(id+"F9.opExtrude","SWEPT_EDGE",EDGE,{"disambiguationData":[OSD([sQuery(id+"F8.wireOp",EDGE,"E48"),sQuery(id+"F8.wireOp",EDGE,"E49")])]});
            var Q5;
            Q5=makeQuery(id+"F9.opExtrude","SWEPT_EDGE",EDGE,{"disambiguationData":[OSD([sQuery(id+"F8.wireOp",EDGE,"E49"),sQuery(id+"F8.wireOp",EDGE,"E50")])]});
            fillet(context, id + "F25", {"entities" : qUnion([Q0, Q1, Q2, Q3, Q4, Q5]), "radius" : 0.81 * mm, "tangentPropagation" : true, "allowEdgeOverflow" : false});
        }
        {
            var Q0;
            Q0=makeQuery(id+"F3.opExtrude","SWEPT_EDGE",EDGE,{"disambiguationData":[OSD([sQuery(id+"F2.wireOp",EDGE,"E22"),sQuery(id+"F2.wireOp",EDGE,"E32")])]});
            var Q1;
            {var subQ0=sQuery(id+"F2.wireOp",EDGE,"E24");var subQ1=sQuery(id+"F2.wireOp",EDGE,"E22");var subQ2=makeQuery(id+"F3.opExtrude","SWEPT_FACE",FACE,{"disambiguationData":[OSD([subQ1,subQ0])]});var subQ3=sQuery(id+"F2.wireOp",EDGE,"E29");var subQ4=sQuery(id+"F2.wireOp",EDGE,"E25");var subQ5=makeQuery(id+"F3.opExtrude","CAP_FACE",FACE,{"disambiguationData":[OSD([subQ1,sQuery(id+"F2.wireOp",EDGE,"E23"),subQ0,subQ4,sQuery(id+"F2.wireOp",EDGE,"E26"),sQuery(id+"F2.wireOp",EDGE,"E27"),sQuery(id+"F2.wireOp",EDGE,"E28"),subQ3,sQuery(id+"F2.wireOp",EDGE,"E30"),sQuery(id+"F2.wireOp",EDGE,"E32"),sQuery(id+"F2.wireOp",EDGE,"E33")])],"isStart":false});var subQ6=makeQuery(id+"F1.opExtrude","SWEPT_FACE",FACE,{"disambiguationData":[OSD([sQuery(id+"F0.wireOp",EDGE,"E17")])]});Q1=makeQuery(id+"F5.boolean.opBoolean","SPLIT",EDGE,{"disambiguationData":[topologyDisambiguationEdgeConnected([subQ6,subQ5,subQ2]),TD([makeQuery(id+"F3.opExtrude","SWEPT_FACE",FACE,{"disambiguationData":[OSD([subQ4])]})])],"derivedFrom":makeQuery(id+"F3.opExtrude","CAP_EDGE",EDGE,{"disambiguationData":[OSD([subQ1,subQ0])],"isStart":false})});}
            var Q2;
            {var subQ0=sQuery(id+"F0.wireOp",EDGE,"E21");var subQ5=sQuery(id+"F2.wireOp",EDGE,"E25");var subQ6=sQuery(id+"F2.wireOp",EDGE,"E24");var subQ7=sQuery(id+"F2.wireOp",EDGE,"E22");var subQ11=sQuery(id+"F0.wireOp",EDGE,"E17");Q2=makeQuery(id+"F22.opFillet","BLEND_EDGE",EDGE,{"blendedFrom":[makeQuery(id+"F3.opExtrude","CAP_EDGE",EDGE,{"disambiguationData":[OSD([subQ5])],"isStart":false}),makeQuery(id+"F5.boolean.opBoolean","SPLIT",FACE,{"disambiguationData":[TD([makeQuery(id+"F1.opExtrude","SWEPT_FACE",FACE,{"disambiguationData":[OSD([subQ0])]})])],"derivedFrom":makeQuery(id+"F3.boolean.opBoolean","MERGE",FACE,{"derivedFrom":[makeQuery(id+"F1.opExtrude","SWEPT_FACE",FACE,{"disambiguationData":[OSD([subQ11])]}),makeQuery(id+"F3.opExtrude","SWEPT_FACE",FACE,{"disambiguationData":[OSD([subQ7,subQ6])]})]})})],"blendedInto":[makeQuery(id+"F5.boolean.opBoolean","SPLIT",FACE,{"disambiguationData":[TD([makeQuery(id+"F1.opExtrude","SWEPT_FACE",FACE,{"disambiguationData":[OSD([subQ0])]})])],"derivedFrom":makeQuery(id+"F3.boolean.opBoolean","MERGE",FACE,{"derivedFrom":[makeQuery(id+"F1.opExtrude","SWEPT_FACE",FACE,{"disambiguationData":[OSD([subQ11])]}),makeQuery(id+"F3.opExtrude","SWEPT_FACE",FACE,{"disambiguationData":[OSD([subQ7,subQ6])]})]})})]});}
            var Q3;
            {var subQ0=sQuery(id+"F2.wireOp",EDGE,"E33");var subQ1=sQuery(id+"F2.wireOp",EDGE,"E32");var subQ2=sQuery(id+"F2.wireOp",EDGE,"E24");var subQ3=sQuery(id+"F2.wireOp",EDGE,"E22");var subQ4=makeQuery(id+"F3.opExtrude","SWEPT_FACE",FACE,{"disambiguationData":[OSD([subQ3,subQ2])]});var subQ5=makeQuery(id+"F3.opExtrude","CAP_FACE",FACE,{"disambiguationData":[OSD([subQ3,sQuery(id+"F2.wireOp",EDGE,"E23"),subQ2,sQuery(id+"F2.wireOp",EDGE,"E25"),sQuery(id+"F2.wireOp",EDGE,"E26"),sQuery(id+"F2.wireOp",EDGE,"E27"),sQuery(id+"F2.wireOp",EDGE,"E28"),sQuery(id+"F2.wireOp",EDGE,"E29"),sQuery(id+"F2.wireOp",EDGE,"E30"),subQ1,subQ0])],"isStart":false});var subQ6=makeQuery(id+"F1.opExtrude","SWEPT_FACE",FACE,{"disambiguationData":[OSD([sQuery(id+"F0.wireOp",EDGE,"E17")])]});var subQ7=sQuery(id+"F4.wireOp",EDGE,"E34.right");Q3=makeQuery(id+"F5.boolean.opBoolean","SPLIT",EDGE,{"disambiguationData":[topologyDisambiguationEdgeConnected([subQ6,subQ5,subQ4]),TD([makeQuery(id+"F5.opExtrude","SWEPT_FACE",FACE,{"disambiguationData":[OSD([subQ7])]})])],"derivedFrom":makeQuery(id+"F3.opExtrude","CAP_EDGE",EDGE,{"disambiguationData":[OSD([subQ3,subQ2])],"isStart":false})});}
            var Q4;
            {var subQ0=sQuery(id+"F2.wireOp",EDGE,"E33");var subQ1=sQuery(id+"F2.wireOp",EDGE,"E32");Q4=makeQuery(id+"F9.boolean.opBoolean","SPLIT",EDGE,{"disambiguationData":[TD([makeQuery(id+"F1.opExtrude","SWEPT_FACE",FACE,{"disambiguationData":[OSD([sQuery(id+"F0.wireOp",EDGE,"E17")])]})])],"derivedFrom":makeQuery(id+"F3.opExtrude","CAP_EDGE",EDGE,{"disambiguationData":[OSD([subQ1,subQ0])],"isStart":false})});}
            var Q5;
            {var subQ2=sQuery(id+"F2.wireOp",EDGE,"E33");var subQ3=sQuery(id+"F2.wireOp",EDGE,"E32");Q5=makeQuery(id+"F9.boolean.opBoolean","SPLIT",EDGE,{"disambiguationData":[TD([makeQuery(id+"F1.opExtrude","SWEPT_FACE",FACE,{"disambiguationData":[OSD([sQuery(id+"F0.wireOp",EDGE,"E16")])]})])],"derivedFrom":makeQuery(id+"F3.opExtrude","CAP_EDGE",EDGE,{"disambiguationData":[OSD([subQ3,subQ2])],"isStart":false})});}
            fillet(context, id + "F26", {"entities" : qUnion([Q0, Q1, Q2, Q3, Q4, Q5]), "radius" : 0.81 * mm, "tangentPropagation" : true, "allowEdgeOverflow" : false});
        }
        {
            var Q0;
            Q0=makeQuery(id+"F3.opExtrude","CAP_EDGE",EDGE,{"disambiguationData":[OSD([sQuery(id+"F2.wireOp",EDGE,"E28")])],"isStart":false});
            var Q1;
            Q1=makeQuery(id+"F3.opExtrude","CAP_EDGE",EDGE,{"disambiguationData":[OSD([sQuery(id+"F2.wireOp",EDGE,"E26")])],"isStart":false});
            var Q2;
            {var subQ1=sQuery(id+"F2.wireOp",EDGE,"E26");var subQ2=sQuery(id+"F2.wireOp",EDGE,"E27");Q2=makeQuery(id+"F9.boolean.opBoolean","SPLIT",EDGE,{"disambiguationData":[TD([makeQuery(id+"F3.opExtrude","SWEPT_FACE",FACE,{"disambiguationData":[OSD([subQ1])]})])],"derivedFrom":makeQuery(id+"F3.opExtrude","CAP_EDGE",EDGE,{"disambiguationData":[OSD([subQ2])],"isStart":false})});}
            var Q3;
            {var subQ1=sQuery(id+"F2.wireOp",EDGE,"E28");var subQ2=sQuery(id+"F2.wireOp",EDGE,"E27");Q3=makeQuery(id+"F9.boolean.opBoolean","SPLIT",EDGE,{"disambiguationData":[TD([makeQuery(id+"F3.opExtrude","SWEPT_FACE",FACE,{"disambiguationData":[OSD([subQ1])]})])],"derivedFrom":makeQuery(id+"F3.opExtrude","CAP_EDGE",EDGE,{"disambiguationData":[OSD([subQ2])],"isStart":false})});}
            var Q4;
            {var subQ0=sQuery(id+"F8.wireOp",EDGE,"E49");Q4=makeQuery(id+"F11.boolean.opBoolean","SPLIT",EDGE,{"disambiguationData":[TD([makeQuery(id+"F9.opExtrude","CAP_FACE",FACE,{"disambiguationData":[OSD([sQuery(id+"F8.wireOp",EDGE,"E47"),sQuery(id+"F8.wireOp",EDGE,"E48"),subQ0,sQuery(id+"F8.wireOp",EDGE,"E50"),sQuery(id+"F8.wireOp",EDGE,"E51")])],"isStart":false}),makeQuery(id+"F9.opExtrude","SWEPT_FACE",FACE,{"disambiguationData":[OSD([subQ0])]}),makeQuery(id+"F11.opExtrude","SWEPT_FACE",FACE,{"disambiguationData":[OSD([sQuery(id+"F10.wireOp",EDGE,"E53")])]}),makeQuery(id+"F11.opExtrude","SWEPT_FACE",FACE,{"disambiguationData":[OSD([sQuery(id+"F10.wireOp",EDGE,"E57.MirrorC")])]})])],"derivedFrom":makeQuery(id+"F9.opExtrude","CAP_EDGE",EDGE,{"disambiguationData":[OSD([subQ0])],"isStart":false})});}
            var Q5;
            Q5=makeQuery(id+"F11.boolean.opBoolean","SPLIT",EDGE,{"disambiguationData":[OD(1.0)],"derivedFrom":makeQuery(id+"F11.opExtrude","CAP_EDGE",EDGE,{"disambiguationData":[OSD([sQuery(id+"F10.wireOp",EDGE,"E57.MirrorC")])],"isStart":true})});
            var Q6;
            Q6=makeQuery(id+"F11.opExtrude","CAP_EDGE",EDGE,{"disambiguationData":[OSD([sQuery(id+"F10.wireOp",EDGE,"E55")])],"isStart":true});
            var Q7;
            Q7=makeQuery(id+"F11.boolean.opBoolean","SPLIT",EDGE,{"disambiguationData":[OD(1.0)],"derivedFrom":makeQuery(id+"F11.opExtrude","CAP_EDGE",EDGE,{"disambiguationData":[OSD([sQuery(id+"F10.wireOp",EDGE,"E53")])],"isStart":true})});
            fillet(context, id + "F27", {"entities" : qUnion([Q0, Q1, Q2, Q3, Q4, Q5, Q6, Q7]), "radius" : 0.5 * mm, "tangentPropagation" : true, "allowEdgeOverflow" : false});
        }
        {
            var Q0;
            Q0=makeQuery(id+"F3.opExtrude","CAP_EDGE",EDGE,{"disambiguationData":[OSD([sQuery(id+"F2.wireOp",EDGE,"E26")])],"isStart":true});
            var Q1;
            Q1=makeQuery(id+"F3.opExtrude","SWEPT_EDGE",EDGE,{"disambiguationData":[OSD([sQuery(id+"F2.wireOp",EDGE,"E26"),sQuery(id+"F2.wireOp",EDGE,"E27")])]});
            var Q2;
            Q2=makeQuery(id+"F3.opExtrude","CAP_EDGE",EDGE,{"disambiguationData":[OSD([sQuery(id+"F2.wireOp",EDGE,"E27")])],"isStart":true});
            var Q3;
            Q3=makeQuery(id+"F3.opExtrude","SWEPT_EDGE",EDGE,{"disambiguationData":[OSD([sQuery(id+"F2.wireOp",EDGE,"E27"),sQuery(id+"F2.wireOp",EDGE,"E28")])]});
            var Q4;
            Q4=makeQuery(id+"F3.opExtrude","CAP_EDGE",EDGE,{"disambiguationData":[OSD([sQuery(id+"F2.wireOp",EDGE,"E28")])],"isStart":true});
            var Q5;
            {var subQ0=sQuery(id+"F2.wireOp",EDGE,"E24");var subQ1=sQuery(id+"F2.wireOp",EDGE,"E22");Q5=makeQuery(id+"F5.boolean.opBoolean","SPLIT",EDGE,{"disambiguationData":[topologyDisambiguationEdgeConnected([makeQuery(id+"F3.opExtrude","CAP_FACE",FACE,{"disambiguationData":[OSD([subQ1,sQuery(id+"F2.wireOp",EDGE,"E23"),subQ0,sQuery(id+"F2.wireOp",EDGE,"E25"),sQuery(id+"F2.wireOp",EDGE,"E26"),sQuery(id+"F2.wireOp",EDGE,"E27"),sQuery(id+"F2.wireOp",EDGE,"E28"),sQuery(id+"F2.wireOp",EDGE,"E29"),sQuery(id+"F2.wireOp",EDGE,"E30"),sQuery(id+"F2.wireOp",EDGE,"E32"),sQuery(id+"F2.wireOp",EDGE,"E33")])],"isStart":false}),makeQuery(id+"F5.opExtrude","CAP_FACE",FACE,{"disambiguationData":[OSD([sQuery(id+"F4.wireOp",EDGE,"E34.bottom"),sQuery(id+"F4.wireOp",EDGE,"E34.top"),sQuery(id+"F4.wireOp",EDGE,"E34.left"),sQuery(id+"F4.wireOp",EDGE,"E34.right")])],"isStart":true})])],"derivedFrom":makeQuery(id+"F3.opExtrude","CAP_EDGE",EDGE,{"disambiguationData":[OSD([subQ1,subQ0])],"isStart":false})});}
            var Q6;
            {var subQ0=sQuery(id+"F2.wireOp",EDGE,"E30");var subQ1=sQuery(id+"F2.wireOp",EDGE,"E23");Q6=makeQuery(id+"F17.boolean.opBoolean","SPLIT",EDGE,{"disambiguationData":[topologyDisambiguationEdgeConnected([makeQuery(id+"F3.opExtrude","CAP_FACE",FACE,{"disambiguationData":[OSD([sQuery(id+"F2.wireOp",EDGE,"E22"),subQ1,sQuery(id+"F2.wireOp",EDGE,"E24"),sQuery(id+"F2.wireOp",EDGE,"E25"),sQuery(id+"F2.wireOp",EDGE,"E26"),sQuery(id+"F2.wireOp",EDGE,"E27"),sQuery(id+"F2.wireOp",EDGE,"E28"),sQuery(id+"F2.wireOp",EDGE,"E29"),subQ0,sQuery(id+"F2.wireOp",EDGE,"E32"),sQuery(id+"F2.wireOp",EDGE,"E33")])],"isStart":false}),makeQuery(id+"F17.opExtrude","CAP_FACE",FACE,{"disambiguationData":[OSD([sQuery(id+"F16.wireOp",EDGE,"E59.bottom"),sQuery(id+"F16.wireOp",EDGE,"E59.top"),sQuery(id+"F16.wireOp",EDGE,"E59.left"),sQuery(id+"F16.wireOp",EDGE,"E59.right")])],"isStart":true})])],"derivedFrom":makeQuery(id+"F3.opExtrude","CAP_EDGE",EDGE,{"disambiguationData":[OSD([subQ1,subQ0])],"isStart":false})});}
            var Q7;
            Q7=makeQuery(id+"F9.boolean.opBoolean","INTERSECT",EDGE,{"derivedFrom":[makeQuery(id+"F3.opExtrude","SWEPT_FACE",FACE,{"disambiguationData":[OSD([sQuery(id+"F2.wireOp",EDGE,"E32"),sQuery(id+"F2.wireOp",EDGE,"E33")])]}),makeQuery(id+"F9.opExtrude","SWEPT_FACE",FACE,{"disambiguationData":[OSD([sQuery(id+"F8.wireOp",EDGE,"E50")])]})]});
            var Q8;
            Q8=makeQuery(id+"F9.boolean.opBoolean","INTERSECT",EDGE,{"derivedFrom":[makeQuery(id+"F3.opExtrude","SWEPT_FACE",FACE,{"disambiguationData":[OSD([sQuery(id+"F2.wireOp",EDGE,"E32"),sQuery(id+"F2.wireOp",EDGE,"E33")])]}),makeQuery(id+"F9.opExtrude","SWEPT_FACE",FACE,{"disambiguationData":[OSD([sQuery(id+"F8.wireOp",EDGE,"E48")])]})]});
            fillet(context, id + "F28", {"entities" : qUnion([Q0, Q1, Q2, Q3, Q4, Q5, Q6, Q7, Q8]), "radius" : 0.5 * mm, "tangentPropagation" : true, "allowEdgeOverflow" : false});
        }
        {
            var Q0;
            {var subQ0=sQuery(id+"F16.wireOp",EDGE,"E59.right");Q0=makeQuery(id+"F17.boolean.opBoolean","SPLIT",EDGE,{"disambiguationData":[topologyDisambiguationEdgeConnected([makeQuery(id+"F17.opExtrude","CAP_FACE",FACE,{"disambiguationData":[OSD([sQuery(id+"F16.wireOp",EDGE,"E59.bottom"),sQuery(id+"F16.wireOp",EDGE,"E59.top"),sQuery(id+"F16.wireOp",EDGE,"E59.left"),subQ0])],"isStart":true})])],"derivedFrom":makeQuery(id+"F17.opExtrude","CAP_EDGE",EDGE,{"disambiguationData":[OSD([subQ0])],"isStart":true})});}
            var Q1;
            Q1=makeQuery(id+"F17.opExtrude","CAP_EDGE",EDGE,{"disambiguationData":[OSD([sQuery(id+"F16.wireOp",EDGE,"E59.top")])],"isStart":true});
            var Q2;
            {var subQ0=sQuery(id+"F16.wireOp",EDGE,"E59.left");Q2=makeQuery(id+"F17.boolean.opBoolean","SPLIT",EDGE,{"disambiguationData":[topologyDisambiguationEdgeConnected([makeQuery(id+"F17.opExtrude","CAP_FACE",FACE,{"disambiguationData":[OSD([sQuery(id+"F16.wireOp",EDGE,"E59.bottom"),sQuery(id+"F16.wireOp",EDGE,"E59.top"),subQ0,sQuery(id+"F16.wireOp",EDGE,"E59.right")])],"isStart":true})])],"derivedFrom":makeQuery(id+"F17.opExtrude","CAP_EDGE",EDGE,{"disambiguationData":[OSD([subQ0])],"isStart":true})});}
            var Q3;
            Q3=makeQuery(id+"F17.opExtrude","SWEPT_EDGE",EDGE,{"disambiguationData":[OSD([sQuery(id+"F16.wireOp",EDGE,"E59.top"),sQuery(id+"F16.wireOp",EDGE,"E59.right")])]});
            var Q4;
            Q4=makeQuery(id+"F17.opExtrude","SWEPT_EDGE",EDGE,{"disambiguationData":[OSD([sQuery(id+"F16.wireOp",EDGE,"E59.top"),sQuery(id+"F16.wireOp",EDGE,"E59.left")])]});
            var Q5;
            {var subQ0=sQuery(id+"F4.wireOp",EDGE,"E34.left");Q5=makeQuery(id+"F5.boolean.opBoolean","SPLIT",EDGE,{"disambiguationData":[topologyDisambiguationEdgeConnected([makeQuery(id+"F5.opExtrude","CAP_FACE",FACE,{"disambiguationData":[OSD([sQuery(id+"F4.wireOp",EDGE,"E34.bottom"),sQuery(id+"F4.wireOp",EDGE,"E34.top"),subQ0,sQuery(id+"F4.wireOp",EDGE,"E34.right")])],"isStart":true})])],"derivedFrom":makeQuery(id+"F5.opExtrude","CAP_EDGE",EDGE,{"disambiguationData":[OSD([subQ0])],"isStart":true})});}
            var Q6;
            Q6=makeQuery(id+"F5.opExtrude","SWEPT_EDGE",EDGE,{"disambiguationData":[OSD([sQuery(id+"F4.wireOp",EDGE,"E34.top"),sQuery(id+"F4.wireOp",EDGE,"E34.left")])]});
            var Q7;
            Q7=makeQuery(id+"F5.opExtrude","CAP_EDGE",EDGE,{"disambiguationData":[OSD([sQuery(id+"F4.wireOp",EDGE,"E34.top")])],"isStart":true});
            var Q8;
            Q8=makeQuery(id+"F5.opExtrude","SWEPT_EDGE",EDGE,{"disambiguationData":[OSD([sQuery(id+"F4.wireOp",EDGE,"E34.top"),sQuery(id+"F4.wireOp",EDGE,"E34.right")])]});
            var Q9;
            {var subQ0=sQuery(id+"F4.wireOp",EDGE,"E34.right");Q9=makeQuery(id+"F5.boolean.opBoolean","SPLIT",EDGE,{"disambiguationData":[topologyDisambiguationEdgeConnected([makeQuery(id+"F5.opExtrude","CAP_FACE",FACE,{"disambiguationData":[OSD([sQuery(id+"F4.wireOp",EDGE,"E34.bottom"),sQuery(id+"F4.wireOp",EDGE,"E34.top"),sQuery(id+"F4.wireOp",EDGE,"E34.left"),subQ0])],"isStart":true})])],"derivedFrom":makeQuery(id+"F5.opExtrude","CAP_EDGE",EDGE,{"disambiguationData":[OSD([subQ0])],"isStart":true})});}
            fillet(context, id + "F29", {"entities" : qUnion([Q0, Q1, Q2, Q3, Q4, Q5, Q6, Q7, Q8, Q9]), "radius" : 0.38 * mm, "tangentPropagation" : true, "allowEdgeOverflow" : false});
        }
    });
